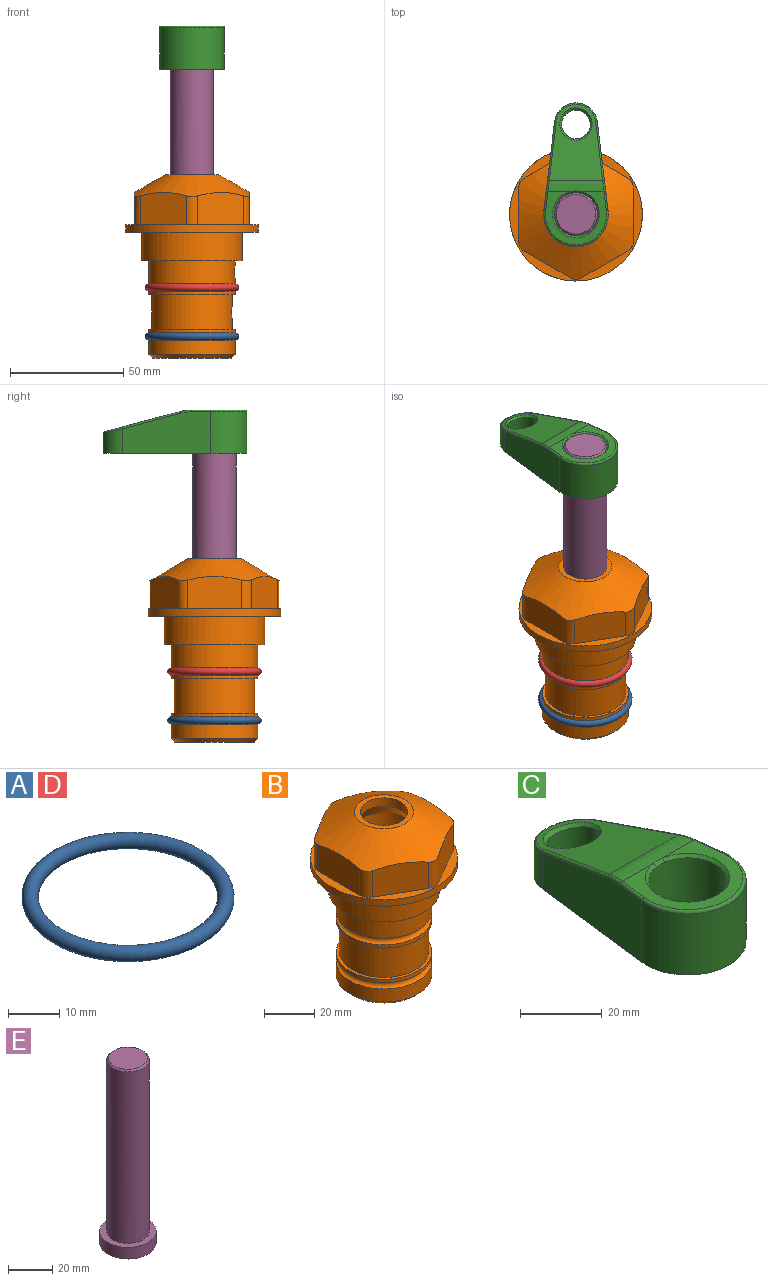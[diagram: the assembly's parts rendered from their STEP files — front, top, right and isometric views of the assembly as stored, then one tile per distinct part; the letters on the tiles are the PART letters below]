
ASSEMBLY  parts=5 mates=4
PART A: 1 faces, bbox 44.7x44.7x3.2 mm
  f0: torus R=19.05mm, axis (0,0,1), area 1193.9mm2
PART B: 36 faces, bbox 58.7x58.7x81 mm
  f0: cylinder r=17.78mm len=35.56mm, axis (0,0,1), area 1670.8mm2, adj f23,f24,f31
  f1: cylinder r=19.05mm len=38.1mm, axis (0,0,1), area 1191.9mm2, adj f26,f27,f30
  f2: plane 58.66x58.66mm, normal (0,0,-1), area 1150.6mm2, adj f3,f28
  f3: cylinder r=29.33mm len=58.66mm, axis (0,0,-1), area 585.1mm2, adj f2,f4
  f4: plane 58.66x58.66mm, normal (0,0,1), area 475.9mm2, adj f3,f5,f6,f7,f8,f9,f10,f11
  f5: plane 20.32x14.34mm, normal (-0.5,0.87,0), area 324.4mm2, adj f4,f15,f16,f17
  f6: plane 20.32x14.34mm, normal (0.5,0.87,0), area 324.4mm2, adj f4,f14,f15,f17
  f7: plane 23.48x14.34mm, normal (1,0,0), area 324.4mm2, adj f4,f13,f14,f17
  f8: plane 20.32x14.34mm, normal (0.5,-0.87,0), area 324.4mm2, adj f4,f12,f13,f17
  f9: plane 20.32x14.34mm, normal (-0.5,-0.87,0), area 324.4mm2, adj f4,f11,f12,f17
  f10: plane 23.48x14.34mm, normal (-1,0,0), area 324.4mm2, adj f4,f11,f16,f17
  f11: cylinder r=5.08mm len=12.85mm, axis (0,0,-1), area 67.2mm2, adj f4,f9,f10,f17
  f12: cylinder r=5.08mm len=12.85mm, axis (0,0,-1), area 67.2mm2, adj f4,f8,f9,f17
  f13: cylinder r=5.08mm len=12.85mm, axis (0,0,-1), area 67.2mm2, adj f4,f7,f8,f17
  f14: cylinder r=5.08mm len=12.85mm, axis (0,0,-1), area 67.2mm2, adj f4,f6,f7,f17
  f15: cylinder r=5.08mm len=12.85mm, axis (0,0,-1), area 67.2mm2, adj f4,f5,f6,f17
  f16: cylinder r=5.08mm len=12.85mm, axis (0,0,-1), area 67.2mm2, adj f4,f5,f10,f17
  f17: cone r=11.73mm half-angle=60deg, axis (0,0,-1), area 2071.8mm2, adj f5,f6,f7,f8,f9,f10,f11,f12
  f18: plane 23.46x23.46mm, normal (0,0,1), area 147.4mm2, adj f17,f35
  f19: plane 34.93x34.93mm, normal (0,0,-1), area 958mm2, adj f29
  f20: cylinder r=19.05mm len=38.1mm, axis (0,0,1), area 760.1mm2, adj f21,f29
  f21: torus R=19.05mm, axis (0,0,1), area 565.3mm2, adj f20,f22
  f22: cylinder r=19.05mm len=38.1mm, axis (0,0,1), area 190mm2, adj f21,f23
  f23: plane 38.1x38.1mm, normal (0,0,1), area 146.9mm2, adj f0,f22
  f24: plane 38.1x38.1mm, normal (0,0,-1), area 146.9mm2, adj f0,f25
  f25: cylinder r=19.05mm len=38.1mm, axis (0,0,1), area 190mm2, adj f24,f26
  f26: torus R=19.05mm, axis (0,0,1), area 565.3mm2, adj f1,f25
  f27: plane 44.45x44.45mm, normal (0,0,-1), area 411.7mm2, adj f1,f28
  f28: cylinder r=22.23mm len=44.45mm, axis (0,0,1), area 1773.5mm2, adj f2,f27
  f29: cone r=19.05mm half-angle=45deg, axis (0,0,1), area 257.5mm2, adj f19,f20
  f30: cylinder r=3.17mm len=6.75mm, axis (-1,0,0), area 128mm2, adj f1,f33
  f31: cylinder r=3.17mm len=6.35mm, axis (-1,0,0), area 102.5mm2, adj f0,f33
  f32: plane 25.4x25.4mm, normal (0,0,1), area 506.7mm2, adj f33
  f33: cylinder r=12.7mm len=66.42mm, axis (0,0,-1), area 5236.2mm2, adj f30,f31,f32,f34
  f34: cone r=9.53mm half-angle=30deg, axis (0,0,-1), area 443.4mm2, adj f33,f35
  f35: cylinder r=9.53mm len=19.05mm, axis (0,0,-1), area 240.9mm2, adj f18,f34
PART C: 31 faces, bbox 31.7x65.5x19.8 mm
  f0: plane 39.12x18.26mm, normal (0.99,0.12,0), area 612.2mm2, adj f1,f4,f7,f11,f13,f15
  f1: cylinder r=9.53mm len=18.91mm, axis (0,0,-1), area 296.1mm2, adj f0,f2,f7,f17
  f2: plane 39.12x18.26mm, normal (-0.99,0.12,0), area 612.2mm2, adj f1,f4,f7,f12,f14,f16
  f3: cylinder r=6.35mm len=12.7mm, axis (0,0,-1), area 362.4mm2, adj f7,f18
  f4: cylinder r=14.29mm len=28.58mm, axis (0,0,-1), area 882.2mm2, adj f0,f2,f7,f10
  f5: cylinder r=9.53mm len=19.05mm, axis (0,0,-1), area 1092.6mm2, adj f7,f19,f20
  f6: plane 26.99x23.69mm, normal (0,0,1), area 216.2mm2, adj f9,f10,f11,f12,f19
  f7: plane 63.5x28.58mm, normal (0,0,-1), area 661.8mm2, adj f0,f1,f2,f3,f4,f5,f22,f23
  f8: plane 33.52x23.6mm, normal (0,0.26,0.97), area 486mm2, adj f9,f15,f16,f17,f18
  f9: cylinder r=19.05mm len=24.72mm, axis (1,0,0), area 120.4mm2, adj f6,f8,f13,f14,f20
  f10: torus R=13.49mm, axis (0,0,1), area 59mm2, adj f4,f6,f11,f12
  f11: cylinder r=0.79mm len=8.67mm, axis (0.12,-0.99,0), area 10.8mm2, adj f0,f6,f10,f13
  f12: cylinder r=0.79mm len=8.67mm, axis (0.12,0.99,0), area 10.8mm2, adj f2,f6,f10,f14
  f13: bspline ~4.95x1.42mm, area 6.1mm2, adj f0,f9,f11,f15
  f14: bspline ~4.95x1.42mm, area 6.1mm2, adj f2,f9,f12,f16
  f15: cylinder r=0.79mm len=25.95mm, axis (0.12,-0.96,0.26), area 32.9mm2, adj f0,f8,f13,f17
  f16: cylinder r=0.79mm len=25.95mm, axis (0.12,0.96,-0.26), area 32.9mm2, adj f2,f8,f14,f17
  f17: bspline ~18.91x8.38mm, area 30mm2, adj f1,f8,f15,f16
  f18: bspline ~14.29x14.29mm, area 48.3mm2, adj f3,f8
  f19: cone r=9.53mm half-angle=45deg, axis (0,0,1), area 66.5mm2, adj f5,f6,f20
  f20: bspline ~3.22x0.96mm, area 3.5mm2, adj f5,f9,f19
  f21: plane 2.75x2.72mm, normal (0,0,-1), area 2.9mm2, adj f23,f25,f28
  f22: plane 23.05x15.88mm, normal (-0.99,-0.12,0), area 323.6mm2, adj f7,f25,f26,f27,f28,f29
  f23: plane 23.05x15.88mm, normal (0.99,-0.12,0), area 323.6mm2, adj f7,f21,f25,f27,f28,f30
  f24: cylinder r=9.53mm len=10.69mm, axis (0,0,-1), area 114.7mm2, adj f7,f27,f29,f30
  f25: cylinder r=12.7mm len=20.59mm, axis (0,0,-1), area 381.1mm2, adj f7,f21,f22,f23,f26,f28
  f26: plane 2.75x2.72mm, normal (0,0,-1), area 2.9mm2, adj f22,f25,f28
  f27: plane 19.72x18.37mm, normal (0,-0.26,-0.97), area 291.8mm2, adj f22,f23,f24,f28,f29,f30
  f28: cylinder r=15.88mm len=19.92mm, axis (1,0,0), area 54.8mm2, adj f21,f22,f23,f25,f26,f27
  f29: cylinder r=1.59mm len=11mm, axis (0,0,-1), area 34.7mm2, adj f7,f22,f24,f27
  f30: cylinder r=1.59mm len=11mm, axis (0,0,-1), area 34.7mm2, adj f7,f23,f24,f27
PART D: same geometry as A
PART E: 6 faces, bbox 25.4x25.4x101.6 mm
  f0: plane 17.46x17.46mm, normal (0,0,1), area 239.5mm2, adj f5
  f1: plane 25.4x25.4mm, normal (0,0,-1), area 506.7mm2, adj f2
  f2: cylinder r=12.7mm len=25.4mm, axis (0,0,1), area 506.7mm2, adj f1,f3
  f3: plane 25.4x25.4mm, normal (0,0,1), area 221.7mm2, adj f2,f4
  f4: cylinder r=9.53mm len=94.46mm, axis (0,0,1), area 5653mm2, adj f3,f5
  f5: cone r=8.73mm half-angle=45deg, axis (0,0,-1), area 64.4mm2, adj f0,f4
PLACE A t=(0,0,-21.59)mm
PLACE B at identity fixed
PLACE C t=(0,0,27.55)mm
PLACE D at identity
PLACE E t=(0,0,27.55)mm
MATE fastened B.f0 <-> D.f0  axis (0,0,1) through (0,0,-24.51)mm
MATE cylindrical E.f2 <-> B.f0  axis (0,0,-1) through (0,0,-10.55)mm
MATE fastened E.f2 <-> C.f4  axis (0,0,1) through (0,0,91.05)mm
MATE fastened B.f0 <-> A.f0  axis (0,0,1) through (0,0,-46.1)mm
